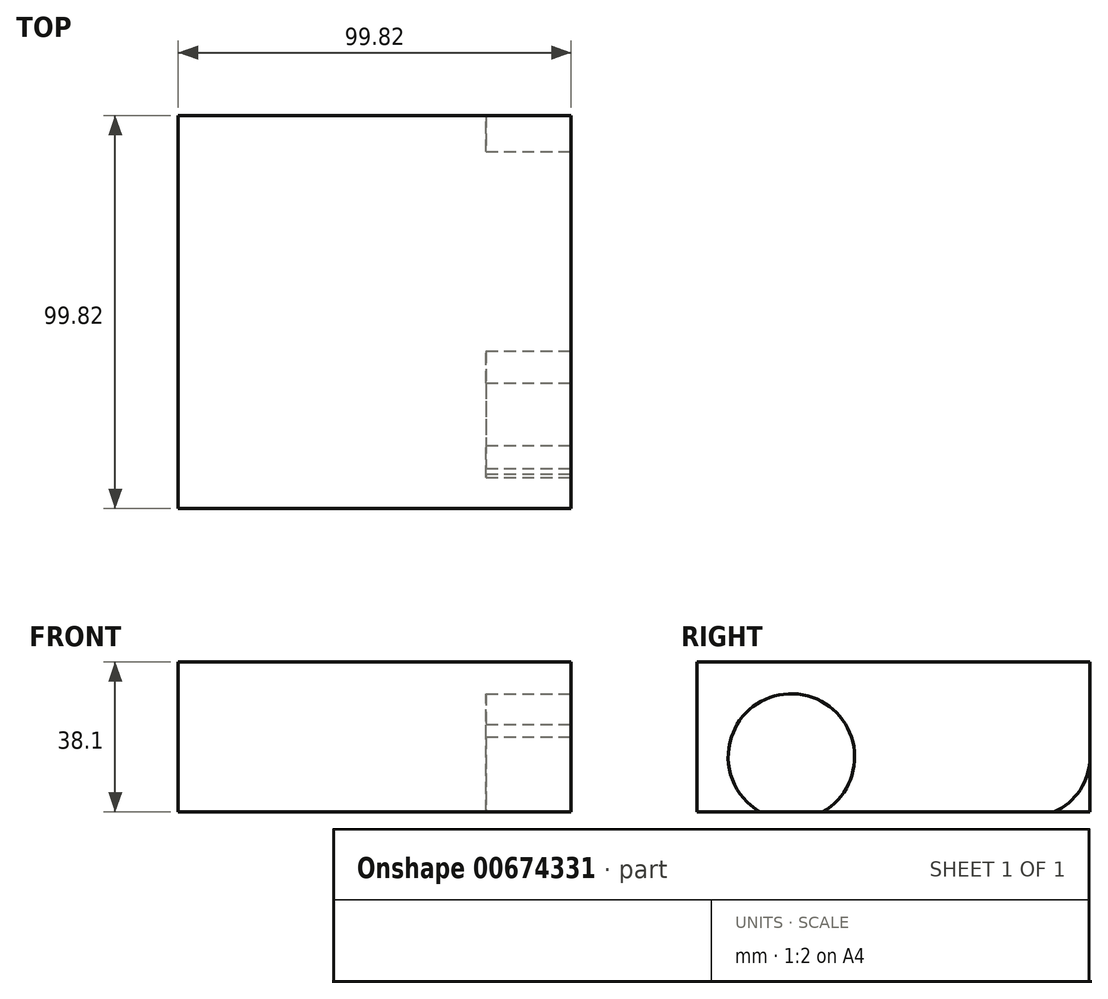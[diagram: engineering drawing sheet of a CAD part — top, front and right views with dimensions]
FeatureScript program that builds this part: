
annotation { "Feature Type Name" : "Feature", "Feature Type Description" : "" }
export const myFeature = defineFeature(function(context is Context, id is Id, definition is map)
    precondition{}
    {
        {
            var Q0;
            Q0=qCreatedBy(makeId("Top.planeOp"),FACE);
            var sketch = newSketch(context, id + "F0", { "sketchPlane" : qUnion([Q0])});
            skLineSegment(sketch, "E0.bottom", {"start": v(49.91, 49.91) * mm, "end": v(-49.91, 49.91) * mm});
            skLineSegment(sketch, "E0.top", {"start": v(49.91, -49.91) * mm, "end": v(-49.91, -49.91) * mm});
            skLineSegment(sketch, "E0.left", {"start": v(49.91, 49.91) * mm, "end": v(49.91, -49.91) * mm});
            skLineSegment(sketch, "E0.right", {"start": v(-49.91, 49.91) * mm, "end": v(-49.91, -49.91) * mm});
            skPoint(sketch, "E0.middle", {"position": v(0, 0) * mm});
            skSolve(sketch);
        }
        {
            var Q0;
            Q0=makeQuery(id+"F0.imprint","IMPRINT",FACE,{"disambiguationData":[TD([[makeQuery(id+"F0.imprint","IMPRINT",EDGE,{"derivedFrom":sQuery(id+"F0.wireOp",EDGE,"E0.bottom")}),1.0]])]});
            extrude(context, id + "F1", {"entities" : qUnion([Q0]), "depth" : 38.1 * mm, "offsetDistance" : 25.4 * mm});
        }
        {
            var Q0;
            Q0=makeQuery(id+"F1.opExtrude","SWEPT_FACE",FACE,{"disambiguationData":[OSD([sQuery(id+"F0.wireOp",EDGE,"E0.left")])]});
            var sketch = newSketch(context, id + "F2", { "sketchPlane" : qUnion([Q0])});
            skLineSegment(sketch, "E1", {"start": v(-49.91, 0) * mm, "end": v(-32.48, 38.1) * mm});
            skLineSegment(sketch, "E2", {"start": v(-32.48, 38.1) * mm, "end": v(-32.48, 0) * mm});
            skLineSegment(sketch, "E3", {"start": v(-41.2, 19.05) * mm, "end": v(-25.96, 19.05) * mm});
            skLineSegment(sketch, "E4", {"start": v(-25.96, 0) * mm, "end": v(-25.96, 13.97) * mm});
            skCircle(sketch, "E5", {"center": v(-25.96, 13.97) * mm, "radius": 16.06 * mm});
            skLineSegment(sketch, "E6", {"start": v(49.91, 13.97) * mm, "end": v(34.67, 13.97) * mm});
            skCircle(sketch, "E7", {"center": v(34.67, 13.97) * mm, "radius": 15.24 * mm});
            skSolve(sketch);
        }
        {
            var Q0;
            {var subQ1=sQuery(id+"F2.wireOp",EDGE,"E3");var subQ5=sQuery(id+"F2.wireOp",EDGE,"E2");var subQ6=makeQuery(id+"F2.imprint","INTERSECT",VERTEX,{"derivedFrom":[subQ5,subQ1]});Q0=makeQuery(id+"F2.imprint","IMPRINT",FACE,{"disambiguationData":[TD([[makeQuery(id+"F2.imprint","IMPRINT",EDGE,{"disambiguationData":[TD([[subQ6,1.0]])],"derivedFrom":subQ5}),-1.0]])]});}
            var Q1;
            {var subQ1=makeQuery(id+"F1.opExtrude","CAP_EDGE",EDGE,{"disambiguationData":[OSD([sQuery(id+"F0.wireOp",EDGE,"E0.left")])],"isStart":true});var subQ3=makeQuery(id+"F2.imprint","IMPRINT",VERTEX,{"derivedFrom":subQ1});Q1=makeQuery(id+"F2.imprint","IMPRINT",FACE,{"disambiguationData":[TD([[makeQuery(id+"F2.imprint","IMPRINT",EDGE,{"disambiguationData":[TD([[subQ3,-1.0]])],"derivedFrom":subQ1}),-1.0]])]});}
            var Q2;
            {var subQ0=sQuery(id+"F2.wireOp",EDGE,"E2");var subQ1=makeQuery(id+"F1.opExtrude","CAP_EDGE",EDGE,{"disambiguationData":[OSD([sQuery(id+"F0.wireOp",EDGE,"E0.left")])],"isStart":true});var subQ2=makeQuery(id+"F2.imprint","INTERSECT",VERTEX,{"derivedFrom":[subQ1,subQ0]});Q2=makeQuery(id+"F2.imprint","IMPRINT",FACE,{"disambiguationData":[TD([[makeQuery(id+"F2.imprint","IMPRINT",EDGE,{"disambiguationData":[TD([[subQ2,1.0]])],"derivedFrom":subQ0}),-1.0]])]});}
            var Q3;
            {var subQ0=sQuery(id+"F2.wireOp",EDGE,"E7");var subQ1=sQuery(id+"F0.wireOp",EDGE,"E0.left");var subQ3=makeQuery(id+"F1.opExtrude","CAP_EDGE",EDGE,{"disambiguationData":[OSD([subQ1])],"isStart":true});var subQ4=makeQuery(id+"F2.imprint","INTERSECT",VERTEX,{"disambiguationData":[OD(0.0)],"derivedFrom":[subQ3,subQ0]});Q3=makeQuery(id+"F2.imprint","IMPRINT",FACE,{"disambiguationData":[TD([[makeQuery(id+"F2.imprint","IMPRINT",EDGE,{"disambiguationData":[TD([[subQ4,1.0]])],"derivedFrom":subQ3}),-1.0]])]});}
            extrude(context, id + "F3", {"entities" : qUnion([Q0, Q1, Q2, Q3]), "operationType" : NewBodyOperationType.REMOVE, "oppositeDirection" : true, "depth" : 21.59 * mm, "offsetDistance" : 25.4 * mm});
        }
    });
